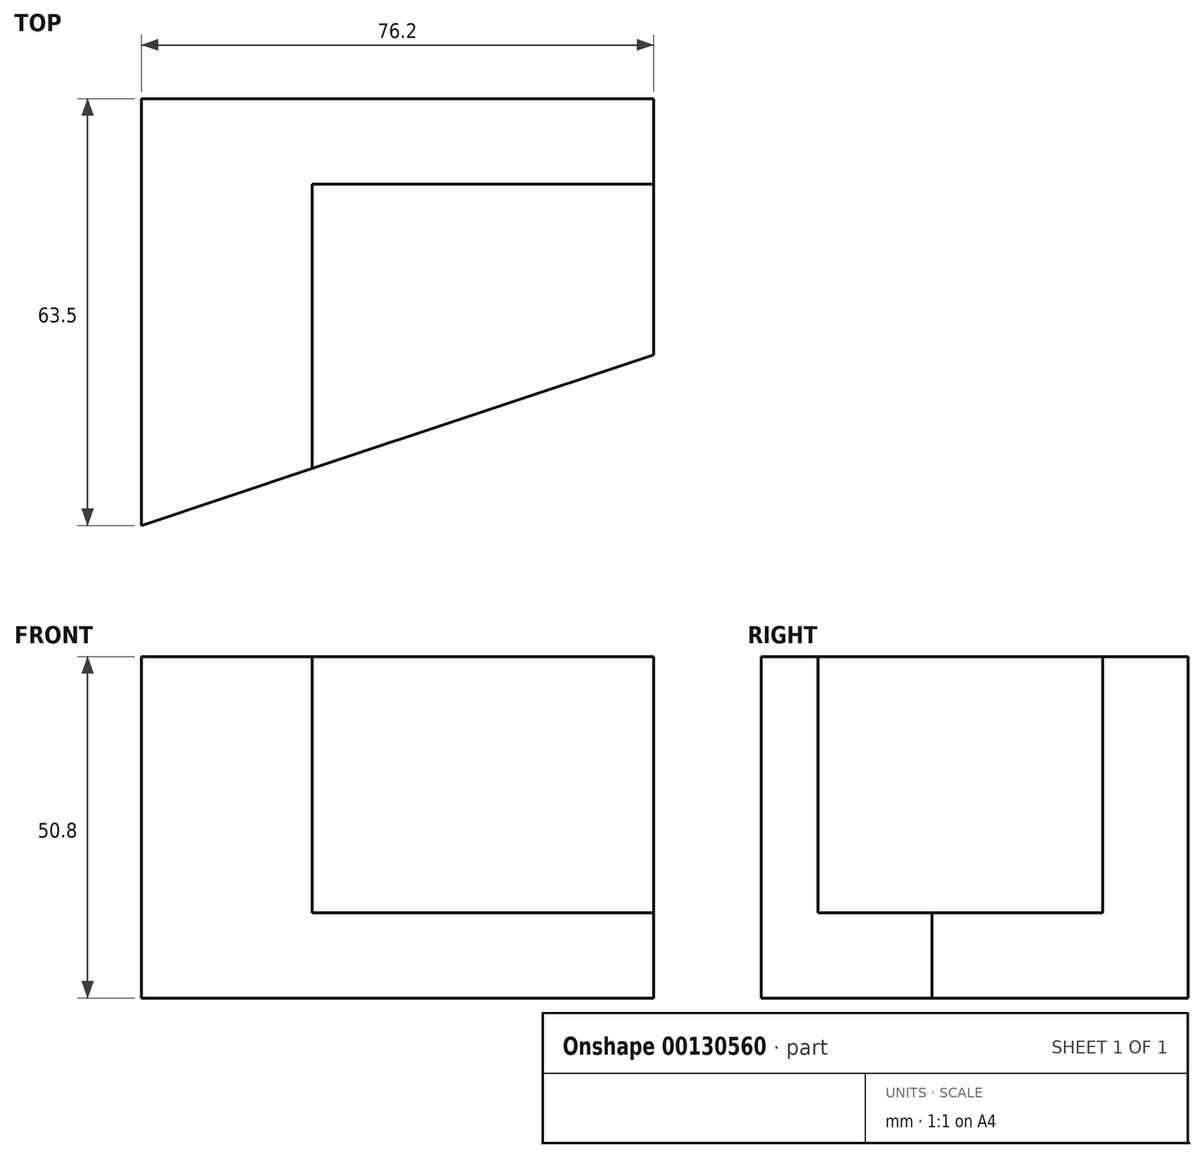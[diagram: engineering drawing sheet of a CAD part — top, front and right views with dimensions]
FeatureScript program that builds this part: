
annotation { "Feature Type Name" : "Feature", "Feature Type Description" : "" }
export const myFeature = defineFeature(function(context is Context, id is Id, definition is map)
    precondition{}
    {
        {
            var Q0;
            Q0=qCreatedBy(makeId("Front.planeOp"),FACE);
            var sketch = newSketch(context, id + "F0", { "sketchPlane" : qUnion([Q0])});
            skLineSegment(sketch, "E0.bottom", {"start": v(38.1, 25.4) * mm, "end": v(-38.1, 25.4) * mm});
            skLineSegment(sketch, "E0.top", {"start": v(38.1, -25.4) * mm, "end": v(-38.1, -25.4) * mm});
            skLineSegment(sketch, "E0.left", {"start": v(38.1, 25.4) * mm, "end": v(38.1, -25.4) * mm});
            skLineSegment(sketch, "E0.right", {"start": v(-38.1, 25.4) * mm, "end": v(-38.1, -25.4) * mm});
            skPoint(sketch, "E0.middle", {"position": v(0, 0) * mm});
            skLineSegment(sketch, "E1", {"start": v(-12.7, 25.4) * mm, "end": v(-12.7, -12.7) * mm});
            skLineSegment(sketch, "E2", {"start": v(-12.7, -12.7) * mm, "end": v(38.1, -12.7) * mm});
            skSolve(sketch);
        }
        {
            var Q0;
            {var subQ2=sQuery(id+"F0.wireOp",EDGE,"E0.top");Q0=makeQuery(id+"F0.imprint","IMPRINT",FACE,{"disambiguationData":[TD([[makeQuery(id+"F0.imprint","IMPRINT",EDGE,{"derivedFrom":subQ2}),-1.0]])]});}
            var Q1;
            {var subQ3=sQuery(id+"F0.wireOp",EDGE,"E1");Q1=makeQuery(id+"F0.imprint","IMPRINT",FACE,{"disambiguationData":[TD([[makeQuery(id+"F0.imprint","IMPRINT",EDGE,{"derivedFrom":subQ3}),1.0]])]});}
            extrude(context, id + "F1", {"entities" : qUnion([Q0, Q1]), "depth" : 63.5 * mm});
        }
        {
            var Q0;
            {var subQ3=sQuery(id+"F0.wireOp",EDGE,"E1");Q0=makeQuery(id+"F0.imprint","IMPRINT",FACE,{"disambiguationData":[TD([[makeQuery(id+"F0.imprint","IMPRINT",EDGE,{"derivedFrom":subQ3}),1.0]])]});}
            extrude(context, id + "F2", {"entities" : qUnion([Q0]), "operationType" : NewBodyOperationType.REMOVE, "depth" : 63.5 * mm, "hasSecondDirection" : true, "secondDirectionOppositeDirection" : false, "secondDirectionDepth" : 12.7 * mm});
        }
        {
            var Q0;
            Q0=makeQuery(id+"F1.opExtrude","SWEPT_FACE",FACE,{"disambiguationData":[OSD([sQuery(id+"F0.wireOp",EDGE,"E0.top")])]});
            var sketch = newSketch(context, id + "F3", { "sketchPlane" : qUnion([Q0])});
            skLineSegment(sketch, "E3", {"start": v(-38.1, 63.5) * mm, "end": v(38.1, 38.1) * mm});
            skLineSegment(sketch, "E4", {"start": v(38.1, 38.1) * mm, "end": v(38.1, 63.5) * mm});
            skLineSegment(sketch, "E5", {"start": v(38.1, 63.5) * mm, "end": v(-38.1, 63.5) * mm});
            skSolve(sketch);
        }
        {
            var Q0;
            Q0 = qSketchRegion(id + "F3", true);
            extrude(context, id + "F4", {"entities" : qUnion([Q0]), "operationType" : NewBodyOperationType.REMOVE, "endBound" : BoundingType.THROUGH_ALL, "oppositeDirection" : true, "depth" : 25.4 * mm});
        }
    });
